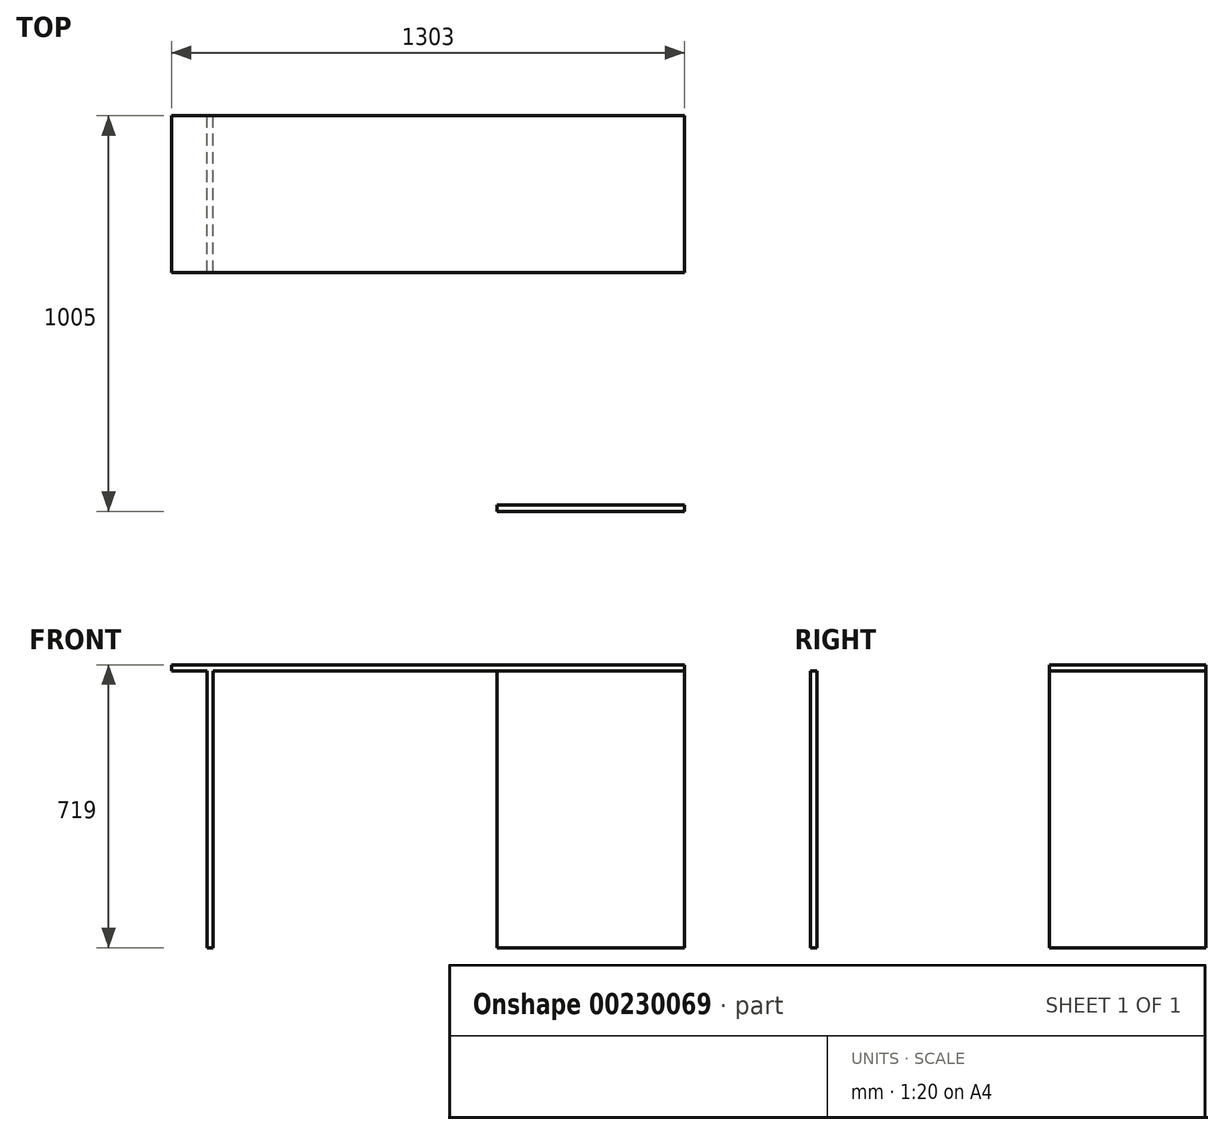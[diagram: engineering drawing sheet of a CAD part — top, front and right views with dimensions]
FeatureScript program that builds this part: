
annotation { "Feature Type Name" : "Feature", "Feature Type Description" : "" }
export const myFeature = defineFeature(function(context is Context, id is Id, definition is map)
    precondition{}
    {
        {
            var Q0;
            Q0=qCreatedBy(makeId("Top.planeOp"),FACE);
            var sketch = newSketch(context, id + "F0", { "sketchPlane" : qUnion([Q0])});
            skLineSegment(sketch, "E0.bottom", {"start": v(-668.67, 219.14) * mm, "end": v(634.33, 219.14) * mm});
            skLineSegment(sketch, "E0.top", {"start": v(-668.67, -178.86) * mm, "end": v(634.33, -178.86) * mm});
            skLineSegment(sketch, "E0.left", {"start": v(-668.67, 219.14) * mm, "end": v(-668.67, -178.86) * mm});
            skLineSegment(sketch, "E0.right", {"start": v(634.33, 219.14) * mm, "end": v(634.33, -178.86) * mm});
            skLineSegment(sketch, "E1.bottom", {"start": v(634.33, -178.86) * mm, "end": v(158.06, -178.86) * mm});
            skLineSegment(sketch, "E1.top", {"start": v(634.33, -1140.86) * mm, "end": v(158.06, -1140.86) * mm});
            skLineSegment(sketch, "E1.left", {"start": v(634.33, -178.86) * mm, "end": v(634.33, -1140.86) * mm});
            skLineSegment(sketch, "E1.right", {"start": v(158.06, -178.86) * mm, "end": v(158.06, -1140.86) * mm});
            skSolve(sketch);
        }
        {
            var Q0;
            Q0=makeQuery(id+"F0.imprint","IMPRINT",FACE,{"disambiguationData":[TD([[makeQuery(id+"F0.imprint","IMPRINT",EDGE,{"derivedFrom":sQuery(id+"F0.wireOp",EDGE,"E0.bottom")}),-1.0]])]});
            var Q1;
            Q1=makeQuery(id+"F0.imprint","IMPRINT",FACE,{"disambiguationData":[TD([[makeQuery(id+"F0.imprint","IMPRINT",EDGE,{"derivedFrom":sQuery(id+"F0.wireOp",EDGE,"E1.bottom")}),1.0]])]});
            extrude(context, id + "F1", {"entities" : qUnion([Q0, Q1]), "depth" : 16 * mm});
        }
        {
            var Q0;
            Q0=makeQuery(id+"F1.opExtrude","CAP_FACE",FACE,{"disambiguationData":[OSD([sQuery(id+"F0.wireOp",EDGE,"E0.bottom"),sQuery(id+"F0.wireOp",EDGE,"E0.top"),sQuery(id+"F0.wireOp",EDGE,"E0.left"),sQuery(id+"F0.wireOp",EDGE,"E0.right"),sQuery(id+"F0.wireOp",EDGE,"E1.top"),sQuery(id+"F0.wireOp",EDGE,"E1.left"),sQuery(id+"F0.wireOp",EDGE,"E1.right")])],"isStart":true});
            var sketch = newSketch(context, id + "F2", { "sketchPlane" : qUnion([Q0])});
            skLineSegment(sketch, "E2.bottom", {"start": v(158.06, 785.86) * mm, "end": v(634.33, 785.86) * mm});
            skLineSegment(sketch, "E2.top", {"start": v(158.06, 769.86) * mm, "end": v(634.33, 769.86) * mm});
            skLineSegment(sketch, "E2.left", {"start": v(158.06, 785.86) * mm, "end": v(158.06, 769.86) * mm});
            skLineSegment(sketch, "E2.right", {"start": v(634.33, 785.86) * mm, "end": v(634.33, 769.86) * mm});
            skLineSegment(sketch, "E3.bottom", {"start": v(-578.67, 178.86) * mm, "end": v(-562.67, 178.86) * mm});
            skLineSegment(sketch, "E3.top", {"start": v(-578.67, -219.14) * mm, "end": v(-562.67, -219.14) * mm});
            skLineSegment(sketch, "E3.left", {"start": v(-578.67, 178.86) * mm, "end": v(-578.67, -219.14) * mm});
            skLineSegment(sketch, "E3.right", {"start": v(-562.67, 178.86) * mm, "end": v(-562.67, -219.14) * mm});
            skSolve(sketch);
        }
        {
            var Q0;
            Q0=makeQuery(id+"F2.imprint","IMPRINT",FACE,{"disambiguationData":[TD([[makeQuery(id+"F2.imprint","IMPRINT",EDGE,{"derivedFrom":sQuery(id+"F2.wireOp",EDGE,"E2.bottom")}),-1.0]])]});
            var Q1;
            Q1=makeQuery(id+"F2.imprint","IMPRINT",FACE,{"disambiguationData":[TD([[makeQuery(id+"F2.imprint","IMPRINT",EDGE,{"derivedFrom":sQuery(id+"F2.wireOp",EDGE,"E3.bottom")}),-1.0]])]});
            extrude(context, id + "F3", {"entities" : qUnion([Q0, Q1]), "operationType" : NewBodyOperationType.ADD, "depth" : 703 * mm});
        }
    });
